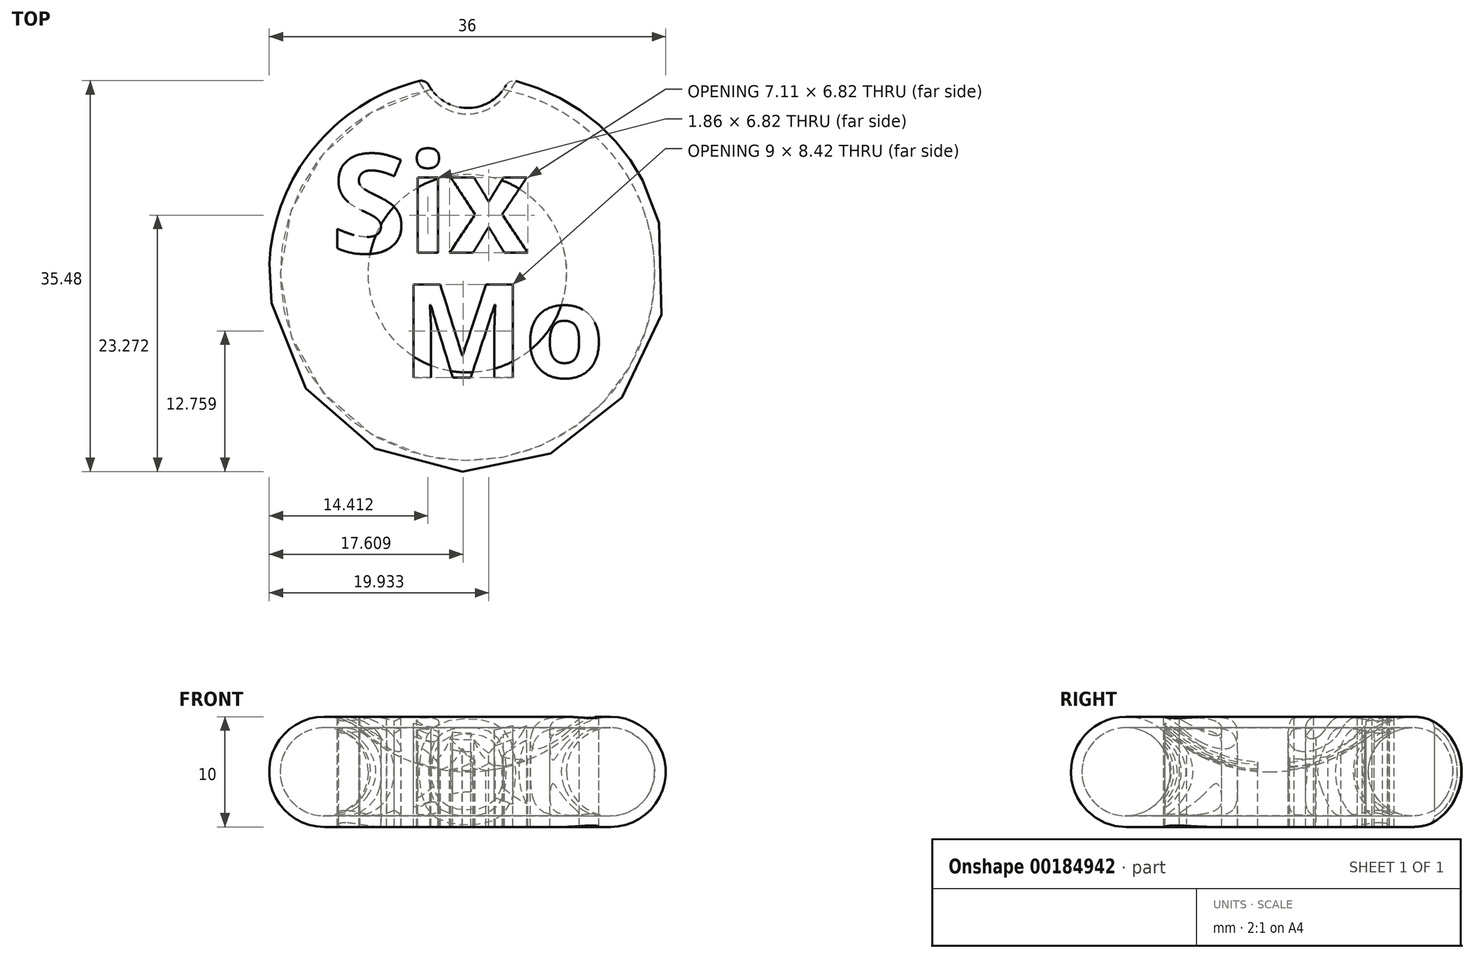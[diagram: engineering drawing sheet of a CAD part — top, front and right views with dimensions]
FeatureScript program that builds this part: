
annotation { "Feature Type Name" : "Feature", "Feature Type Description" : "" }
export const myFeature = defineFeature(function(context is Context, id is Id, definition is map)
    precondition{}
    {
        {
            var Q0;
            Q0=qCreatedBy(makeId("Front.planeOp"),FACE);
            var sketch = newSketch(context, id + "F0", { "sketchPlane" : qUnion([Q0])});
            skArc(sketch, "E0", {"start": v(-9.65, 8.71) * mm, "mid": v(-17.67, 6.8) * mm, "end": v(-13, 0) * mm});
            skArc(sketch, "E1", {"start": v(-9.65, 8.71) * mm, "mid": v(-5.17, 5.96) * mm, "end": v(0, 5) * mm});
            skLineSegment(sketch, "E2", {"start": v(-13, 0) * mm, "end": v(0, 0) * mm});
            skLineSegment(sketch, "E3", {"start": v(0, 0) * mm, "end": v(0, 5) * mm});
            skSolve(sketch);
        }
        {
            var Q0;
            Q0=makeQuery(id+"F0.imprint","IMPRINT",FACE,{"disambiguationData":[TD([[makeQuery(id+"F0.imprint","IMPRINT",EDGE,{"derivedFrom":sQuery(id+"F0.wireOp",EDGE,"E0")}),1.0]])]});
            var Q1;
            Q1=sQuery(id+"F0.wireOp",EDGE,"E3");
            revolve(context, id + "F1", {"entities" : qUnion([Q0]), "axis" : qUnion([Q1]), "revolveType" : RevolveType.FULL});
        }
        {
            var Q0;
            Q0=qCreatedBy(makeId("Top.planeOp"),FACE);
            cPlane(context, id + "F2", {"entities" : qUnion([Q0]), "cplaneType" : CPlaneType.OFFSET, "offset" : 15 * mm, "width" : 150 * mm, "height" : 150 * mm});
        }
        {
            var Q0;
            Q0=qCreatedBy(id+"F2.planeOp",FACE);
            var sketch = newSketch(context, id + "F3", { "sketchPlane" : qUnion([Q0])});
            skText(sketch, "E4", { "text": "Six", "fontName": "OpenSans-Bold.ttf"});
            skText(sketch, "E5", { "text": "Mo", "fontName": "OpenSans-Bold.ttf"});
            const initialGuessF3  = {"E4": [-0.01238, 0.00186, 1, 0, 0.009], "E5": [-0.00595, -0.00945, 1, 0, 0.00849]};
            skSetInitialGuess(sketch, initialGuessF3);
            skSolve(sketch);
        }
        {
            var Q0;
            Q0=makeQuery(id+"F3.imprint","IMPRINT",FACE,{"disambiguationData":[TD([[makeQuery(id+"F3.imprint","IMPRINT",EDGE,{"derivedFrom":sQuery(id+"F3.wireOp",EDGE,"E4.sketch_text.stroke-0")}),-1.0]])]});
            var Q1;
            Q1=makeQuery(id+"F3.imprint","IMPRINT",FACE,{"disambiguationData":[TD([[makeQuery(id+"F3.imprint","IMPRINT",EDGE,{"derivedFrom":sQuery(id+"F3.wireOp",EDGE,"E4.sketch_text.stroke-33")}),-1.0]])]});
            var Q2;
            Q2=makeQuery(id+"F3.imprint","IMPRINT",FACE,{"disambiguationData":[TD([[makeQuery(id+"F3.imprint","IMPRINT",EDGE,{"derivedFrom":sQuery(id+"F3.wireOp",EDGE,"E4.sketch_text.stroke-28")}),-1.0]])]});
            var Q3;
            Q3=makeQuery(id+"F3.imprint","IMPRINT",FACE,{"disambiguationData":[TD([[makeQuery(id+"F3.imprint","IMPRINT",EDGE,{"derivedFrom":sQuery(id+"F3.wireOp",EDGE,"E4.sketch_text.stroke-37")}),-1.0]])]});
            var Q4;
            Q4=makeQuery(id+"F3.imprint","IMPRINT",FACE,{"disambiguationData":[TD([[makeQuery(id+"F3.imprint","IMPRINT",EDGE,{"derivedFrom":sQuery(id+"F3.wireOp",EDGE,"E5.sketch_text.stroke-0")}),-1.0]])]});
            var Q5;
            Q5=makeQuery(id+"F3.imprint","IMPRINT",FACE,{"disambiguationData":[TD([[makeQuery(id+"F3.imprint","IMPRINT",EDGE,{"derivedFrom":sQuery(id+"F3.wireOp",EDGE,"E5.sketch_text.stroke-19")}),-1.0]])]});
            extrude(context, id + "F4", {"entities" : qUnion([Q0, Q1, Q2, Q3, Q4, Q5]), "operationType" : NewBodyOperationType.REMOVE, "oppositeDirection" : true, "depth" : 25 * mm});
        }
        {
            var Q0;
            Q0=qCreatedBy(makeId("Front.planeOp"),FACE);
            var sketch = newSketch(context, id + "F5", { "sketchPlane" : qUnion([Q0])});
            skCircle(sketch, "E6", {"center": v(-13, 5) * mm, "radius": 4 * mm});
            skSolve(sketch);
        }
        {
            var Q0;
            Q0 = qSketchRegion(id + "F5", true);
            var Q1;
            Q1=sQuery(id+"F0.wireOp",EDGE,"E3");
            revolve(context, id + "F6", {"entities" : qUnion([Q0]), "axis" : qUnion([Q1]), "revolveType" : RevolveType.FULL});
        }
        {
            var Q0;
            Q0=qCreatedBy(makeId("Top.planeOp"),FACE);
            var sketch = newSketch(context, id + "F7", { "sketchPlane" : qUnion([Q0])});
            skCircle(sketch, "E7", {"center": v(0, 19) * mm, "radius": 4 * mm});
            skSolve(sketch);
        }
        {
            var Q0;
            Q0 = qSketchRegion(id + "F7", true);
            extrude(context, id + "F8", {"entities" : qUnion([Q0]), "operationType" : NewBodyOperationType.REMOVE, "depth" : 25 * mm});
        }
        {
            var Q0;
            Q0=makeQuery(id+"F8.boolean.opBoolean","INTERSECT",EDGE,{"derivedFrom":[makeQuery(id+"F4.boolean.opBoolean","SPLIT",FACE,{"disambiguationData":[TD([makeQuery(id+"F1.opRevolve","SWEPT_FACE",FACE,{"disambiguationData":[OSD([sQuery(id+"F0.wireOp",EDGE,"E1")])]}),makeQuery(id+"F1.opRevolve","SWEPT_FACE",FACE,{"disambiguationData":[OSD([sQuery(id+"F0.wireOp",EDGE,"E2")])]}),makeQuery(id+"F4.opExtrude","SWEPT_FACE",FACE,{"disambiguationData":[OSD([sQuery(id+"F3.wireOp",EDGE,"E4.sketch_text.stroke-2")])]}),makeQuery(id+"F4.opExtrude","SWEPT_FACE",FACE,{"disambiguationData":[OSD([sQuery(id+"F3.wireOp",EDGE,"E4.sketch_text.stroke-3")])]}),makeQuery(id+"F4.opExtrude","SWEPT_FACE",FACE,{"disambiguationData":[OSD([sQuery(id+"F3.wireOp",EDGE,"E4.sketch_text.stroke-4")])]}),makeQuery(id+"F4.opExtrude","SWEPT_FACE",FACE,{"disambiguationData":[OSD([sQuery(id+"F3.wireOp",EDGE,"E4.sketch_text.stroke-5")])]}),makeQuery(id+"F4.opExtrude","SWEPT_FACE",FACE,{"disambiguationData":[OSD([sQuery(id+"F3.wireOp",EDGE,"E4.sketch_text.stroke-6")])]}),makeQuery(id+"F4.opExtrude","SWEPT_FACE",FACE,{"disambiguationData":[OSD([sQuery(id+"F3.wireOp",EDGE,"E4.sketch_text.stroke-9")])]}),makeQuery(id+"F4.opExtrude","SWEPT_FACE",FACE,{"disambiguationData":[OSD([sQuery(id+"F3.wireOp",EDGE,"E4.sketch_text.stroke-10")])]}),makeQuery(id+"F4.opExtrude","SWEPT_FACE",FACE,{"disambiguationData":[OSD([sQuery(id+"F3.wireOp",EDGE,"E4.sketch_text.stroke-11")])]}),makeQuery(id+"F4.opExtrude","SWEPT_FACE",FACE,{"disambiguationData":[OSD([sQuery(id+"F3.wireOp",EDGE,"E4.sketch_text.stroke-12")])]}),makeQuery(id+"F4.opExtrude","SWEPT_FACE",FACE,{"disambiguationData":[OSD([sQuery(id+"F3.wireOp",EDGE,"E4.sketch_text.stroke-13")])]}),makeQuery(id+"F4.opExtrude","SWEPT_FACE",FACE,{"disambiguationData":[OSD([sQuery(id+"F3.wireOp",EDGE,"E4.sketch_text.stroke-14")])]}),makeQuery(id+"F4.opExtrude","SWEPT_FACE",FACE,{"disambiguationData":[OSD([sQuery(id+"F3.wireOp",EDGE,"E4.sketch_text.stroke-15")])]}),makeQuery(id+"F4.opExtrude","SWEPT_FACE",FACE,{"disambiguationData":[OSD([sQuery(id+"F3.wireOp",EDGE,"E4.sketch_text.stroke-16")])]}),makeQuery(id+"F4.opExtrude","SWEPT_FACE",FACE,{"disambiguationData":[OSD([sQuery(id+"F3.wireOp",EDGE,"E4.sketch_text.stroke-17")])]}),makeQuery(id+"F4.opExtrude","SWEPT_FACE",FACE,{"disambiguationData":[OSD([sQuery(id+"F3.wireOp",EDGE,"E4.sketch_text.stroke-18")])]}),makeQuery(id+"F4.opExtrude","SWEPT_FACE",FACE,{"disambiguationData":[OSD([sQuery(id+"F3.wireOp",EDGE,"E4.sketch_text.stroke-19")])]}),makeQuery(id+"F4.opExtrude","SWEPT_FACE",FACE,{"disambiguationData":[OSD([sQuery(id+"F3.wireOp",EDGE,"E4.sketch_text.stroke-20")])]}),makeQuery(id+"F4.opExtrude","SWEPT_FACE",FACE,{"disambiguationData":[OSD([sQuery(id+"F3.wireOp",EDGE,"E4.sketch_text.stroke-21")])]}),makeQuery(id+"F4.opExtrude","SWEPT_FACE",FACE,{"disambiguationData":[OSD([sQuery(id+"F3.wireOp",EDGE,"E4.sketch_text.stroke-22")])]}),makeQuery(id+"F4.opExtrude","SWEPT_FACE",FACE,{"disambiguationData":[OSD([sQuery(id+"F3.wireOp",EDGE,"E4.sketch_text.stroke-23")])]}),makeQuery(id+"F4.opExtrude","SWEPT_FACE",FACE,{"disambiguationData":[OSD([sQuery(id+"F3.wireOp",EDGE,"E4.sketch_text.stroke-24")])]}),makeQuery(id+"F4.opExtrude","SWEPT_FACE",FACE,{"disambiguationData":[OSD([sQuery(id+"F3.wireOp",EDGE,"E4.sketch_text.stroke-25")])]}),makeQuery(id+"F4.opExtrude","SWEPT_FACE",FACE,{"disambiguationData":[OSD([sQuery(id+"F3.wireOp",EDGE,"E4.sketch_text.stroke-26")])]}),makeQuery(id+"F4.opExtrude","SWEPT_FACE",FACE,{"disambiguationData":[OSD([sQuery(id+"F3.wireOp",EDGE,"E4.sketch_text.stroke-28")])]}),makeQuery(id+"F4.opExtrude","SWEPT_FACE",FACE,{"disambiguationData":[OSD([sQuery(id+"F3.wireOp",EDGE,"E4.sketch_text.stroke-29")])]}),makeQuery(id+"F4.opExtrude","SWEPT_FACE",FACE,{"disambiguationData":[OSD([sQuery(id+"F3.wireOp",EDGE,"E4.sketch_text.stroke-30")])]}),makeQuery(id+"F4.opExtrude","SWEPT_FACE",FACE,{"disambiguationData":[OSD([sQuery(id+"F3.wireOp",EDGE,"E4.sketch_text.stroke-31")])]}),makeQuery(id+"F4.opExtrude","SWEPT_FACE",FACE,{"disambiguationData":[OSD([sQuery(id+"F3.wireOp",EDGE,"E4.sketch_text.stroke-32")])]}),makeQuery(id+"F4.opExtrude","SWEPT_FACE",FACE,{"disambiguationData":[OSD([sQuery(id+"F3.wireOp",EDGE,"E4.sketch_text.stroke-34")])]}),makeQuery(id+"F4.opExtrude","SWEPT_FACE",FACE,{"disambiguationData":[OSD([sQuery(id+"F3.wireOp",EDGE,"E4.sketch_text.stroke-35")])]}),makeQuery(id+"F4.opExtrude","SWEPT_FACE",FACE,{"disambiguationData":[OSD([sQuery(id+"F3.wireOp",EDGE,"E4.sketch_text.stroke-41")])]}),makeQuery(id+"F4.opExtrude","SWEPT_FACE",FACE,{"disambiguationData":[OSD([sQuery(id+"F3.wireOp",EDGE,"E4.sketch_text.stroke-42")])]}),makeQuery(id+"F4.opExtrude","SWEPT_FACE",FACE,{"disambiguationData":[OSD([sQuery(id+"F3.wireOp",EDGE,"E5.sketch_text.stroke-3")])]}),makeQuery(id+"F4.opExtrude","SWEPT_FACE",FACE,{"disambiguationData":[OSD([sQuery(id+"F3.wireOp",EDGE,"E5.sketch_text.stroke-4")])]}),makeQuery(id+"F4.opExtrude","SWEPT_FACE",FACE,{"disambiguationData":[OSD([sQuery(id+"F3.wireOp",EDGE,"E5.sketch_text.stroke-5")])]}),makeQuery(id+"F4.opExtrude","SWEPT_FACE",FACE,{"disambiguationData":[OSD([sQuery(id+"F3.wireOp",EDGE,"E5.sketch_text.stroke-11")])]}),makeQuery(id+"F4.opExtrude","SWEPT_FACE",FACE,{"disambiguationData":[OSD([sQuery(id+"F3.wireOp",EDGE,"E5.sketch_text.stroke-12")])]}),makeQuery(id+"F4.opExtrude","SWEPT_FACE",FACE,{"disambiguationData":[OSD([sQuery(id+"F3.wireOp",EDGE,"E5.sketch_text.stroke-13")])]}),makeQuery(id+"F4.opExtrude","SWEPT_FACE",FACE,{"disambiguationData":[OSD([sQuery(id+"F3.wireOp",EDGE,"E5.sketch_text.stroke-27")])]}),makeQuery(id+"F4.opExtrude","SWEPT_FACE",FACE,{"disambiguationData":[OSD([sQuery(id+"F3.wireOp",EDGE,"E5.sketch_text.stroke-28")])]}),makeQuery(id+"F4.opExtrude","SWEPT_FACE",FACE,{"disambiguationData":[OSD([sQuery(id+"F3.wireOp",EDGE,"E5.sketch_text.stroke-29")])]}),makeQuery(id+"F4.opExtrude","SWEPT_FACE",FACE,{"disambiguationData":[OSD([sQuery(id+"F3.wireOp",EDGE,"E5.sketch_text.stroke-30")])]}),makeQuery(id+"F4.opExtrude","SWEPT_FACE",FACE,{"disambiguationData":[OSD([sQuery(id+"F3.wireOp",EDGE,"E5.sketch_text.stroke-31")])]}),makeQuery(id+"F4.opExtrude","SWEPT_FACE",FACE,{"disambiguationData":[OSD([sQuery(id+"F3.wireOp",EDGE,"E5.sketch_text.stroke-34")])]}),makeQuery(id+"F4.opExtrude","SWEPT_FACE",FACE,{"disambiguationData":[OSD([sQuery(id+"F3.wireOp",EDGE,"E5.sketch_text.stroke-35")])]}),makeQuery(id+"F4.opExtrude","SWEPT_FACE",FACE,{"disambiguationData":[OSD([sQuery(id+"F3.wireOp",EDGE,"E5.sketch_text.stroke-36")])]})])],"derivedFrom":makeQuery(id+"F1.opRevolve","SWEPT_FACE",FACE,{"disambiguationData":[OSD([sQuery(id+"F0.wireOp",EDGE,"E0")])]})}),makeQuery(id+"F8.opExtrude","SWEPT_FACE",FACE,{"disambiguationData":[OSD([sQuery(id+"F7.wireOp",EDGE,"E7")])]})]});
            fillet(context, id + "F9", {"entities" : qUnion([Q0]), "radius" : .8 * mm, "tangentPropagation" : true, "allowEdgeOverflow" : false});
        }
    });
